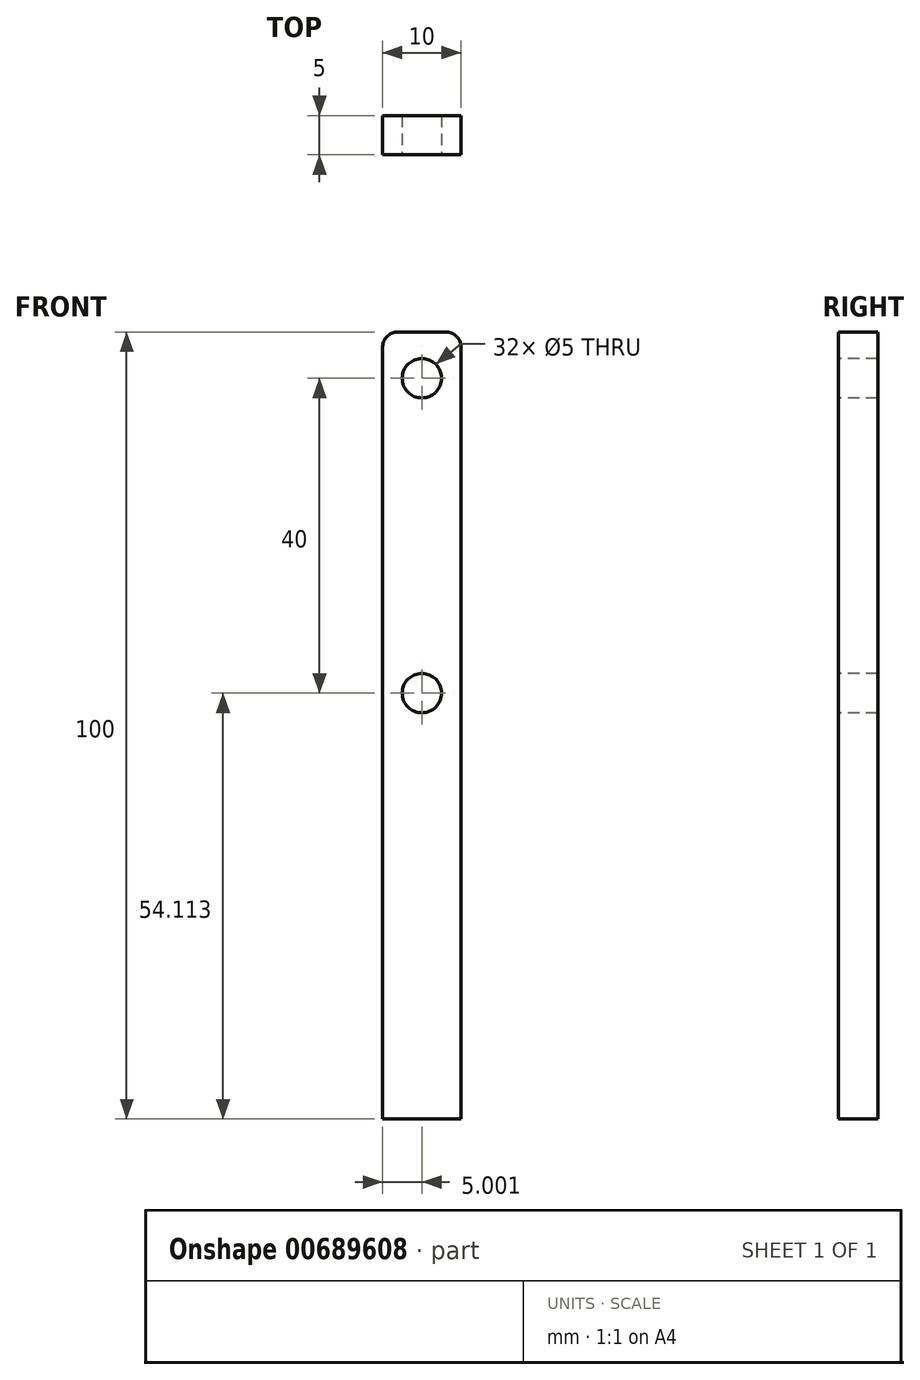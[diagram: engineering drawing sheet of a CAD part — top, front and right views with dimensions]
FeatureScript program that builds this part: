
annotation { "Feature Type Name" : "Feature", "Feature Type Description" : "" }
export const myFeature = defineFeature(function(context is Context, id is Id, definition is map)
    precondition{}
    {
        {
            var Q0;
            Q0=qCreatedBy(makeId("Front.planeOp"),FACE);
            var sketch = newSketch(context, id + "F0", { "sketchPlane" : qUnion([Q0])});
            skLineSegment(sketch, "E0.bottom", {"start": v(-23.3, 67) * mm, "end": v(-13.3, 67) * mm});
            skLineSegment(sketch, "E0.top", {"start": v(-23.3, -33) * mm, "end": v(-13.3, -33) * mm});
            skLineSegment(sketch, "E0.left", {"start": v(-23.3, 67) * mm, "end": v(-23.3, -33) * mm});
            skLineSegment(sketch, "E0.right", {"start": v(-13.3, 67) * mm, "end": v(-13.3, -33) * mm});
            skCircle(sketch, "E1", {"center": v(-18.3, 61.11) * mm, "radius": 2.5 * mm});
            skPoint(sketch, "E1.centerSnap0", {"position": v(-18.3, 67) * mm});
            skCircle(sketch, "E2", {"center": v(-18.3, 21.11) * mm, "radius": 2.5 * mm});
            skSolve(sketch);
        }
        {
            var Q0;
            Q0=makeQuery(id+"F0.imprint","IMPRINT",FACE,{"disambiguationData":[TD([[makeQuery(id+"F0.imprint","IMPRINT",EDGE,{"derivedFrom":sQuery(id+"F0.wireOp",EDGE,"E0.bottom")}),-1.0]])]});
            extrude(context, id + "F1", {"entities" : qUnion([Q0]), "oppositeDirection" : true, "depth" : 5 * mm, "offsetDistance" : 25 * mm});
        }
        {
            var Q0;
            Q0=makeQuery(id+"F1.opExtrude","SWEPT_EDGE",EDGE,{"disambiguationData":[OSD([sQuery(id+"F0.wireOp",EDGE,"E0.bottom"),sQuery(id+"F0.wireOp",EDGE,"E0.right")])]});
            var Q1;
            Q1=makeQuery(id+"F1.opExtrude","SWEPT_EDGE",EDGE,{"disambiguationData":[OSD([sQuery(id+"F0.wireOp",EDGE,"E0.bottom"),sQuery(id+"F0.wireOp",EDGE,"E0.left")])]});
            fillet(context, id + "F2", {"entities" : qUnion([Q0, Q1]), "radius" : 2 * mm, "tangentPropagation" : true, "allowEdgeOverflow" : false});
        }
    });
